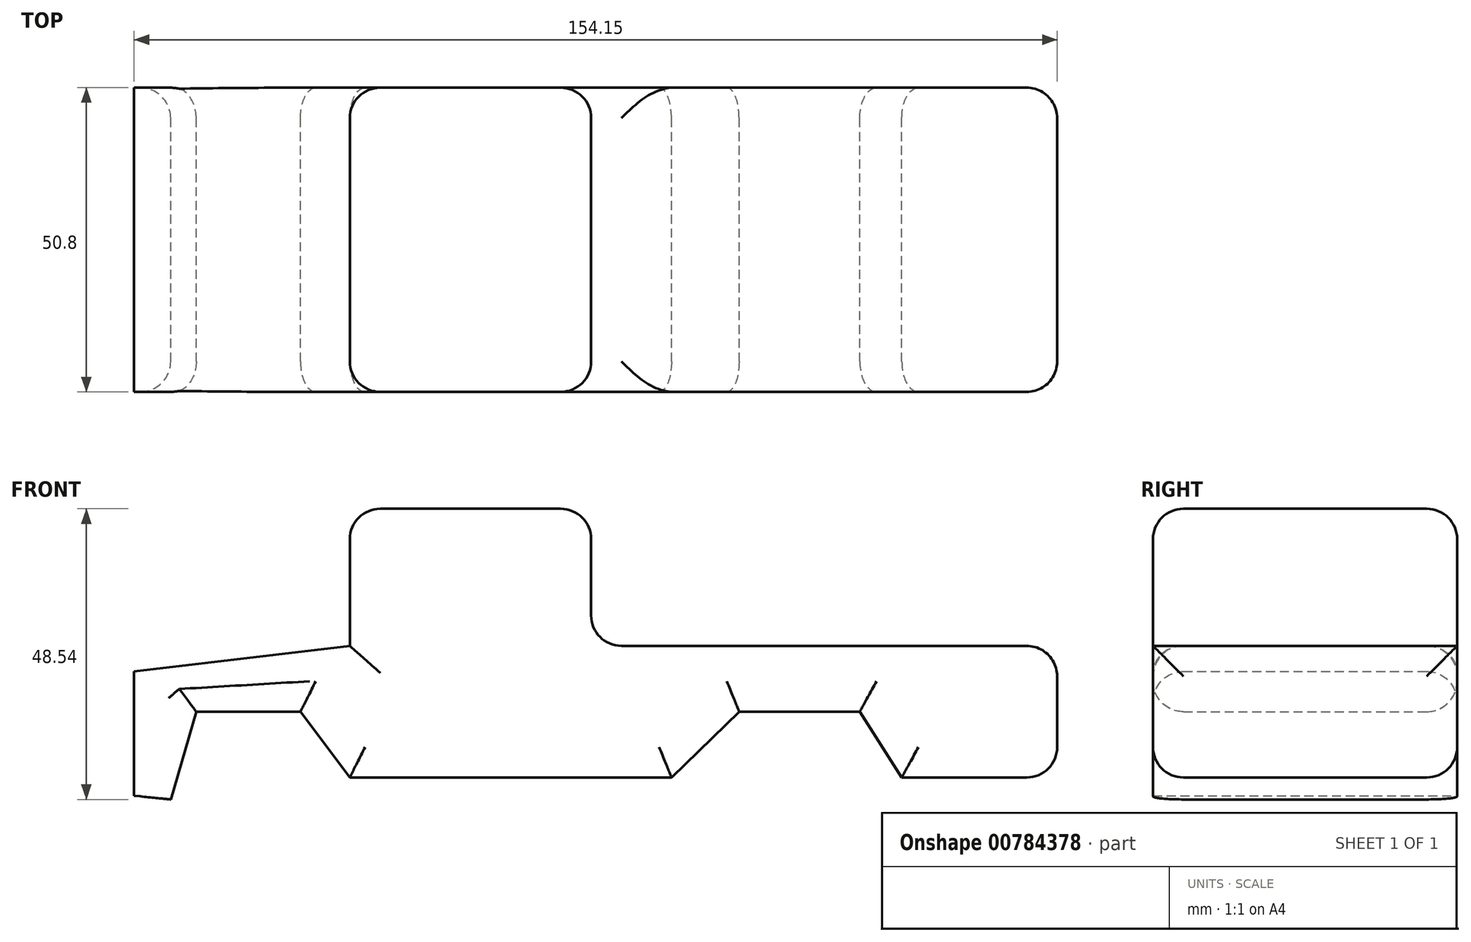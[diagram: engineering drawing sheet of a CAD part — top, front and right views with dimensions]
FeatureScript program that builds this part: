
annotation { "Feature Type Name" : "Feature", "Feature Type Description" : "" }
export const myFeature = defineFeature(function(context is Context, id is Id, definition is map)
    precondition{}
    {
        {
            var Q0;
            Q0=qCreatedBy(makeId("Front.planeOp"),FACE);
            var sketch = newSketch(context, id + "F0", { "sketchPlane" : qUnion([Q0])});
            skLineSegment(sketch, "E0", {"start": v(-106.12, -9.45) * mm, "end": v(-106.12, 11.31) * mm});
            skLineSegment(sketch, "E1", {"start": v(-106.12, 11.31) * mm, "end": v(-70.1, 15.58) * mm});
            skLineSegment(sketch, "E2", {"start": v(-70.1, 15.58) * mm, "end": v(-70.1, 38.48) * mm});
            skLineSegment(sketch, "E3", {"start": v(-70.1, 38.48) * mm, "end": v(-29.81, 38.48) * mm});
            skLineSegment(sketch, "E4", {"start": v(-29.81, 38.48) * mm, "end": v(-29.81, 15.58) * mm});
            skLineSegment(sketch, "E5", {"start": v(-29.81, 15.58) * mm, "end": v(48.03, 15.58) * mm});
            skLineSegment(sketch, "E6", {"start": v(48.03, 15.58) * mm, "end": v(48.03, -6.4) * mm});
            skLineSegment(sketch, "E7", {"start": v(48.03, -6.4) * mm, "end": v(22.08, -6.4) * mm});
            skLineSegment(sketch, "E8", {"start": v(22.08, -6.4) * mm, "end": v(15.06, 4.6) * mm});
            skLineSegment(sketch, "E9", {"start": v(15.06, 4.6) * mm, "end": v(-5.09, 4.6) * mm});
            skLineSegment(sketch, "E10", {"start": v(-5.09, 4.6) * mm, "end": v(-16.38, -6.4) * mm});
            skLineSegment(sketch, "E11", {"start": v(-16.38, -6.4) * mm, "end": v(-70.1, -6.4) * mm});
            skLineSegment(sketch, "E12", {"start": v(-70.1, -6.4) * mm, "end": v(-78.34, 4.6) * mm});
            skLineSegment(sketch, "E13", {"start": v(-78.34, 4.6) * mm, "end": v(-95.74, 4.6) * mm});
            skLineSegment(sketch, "E14", {"start": v(-95.74, 4.6) * mm, "end": v(-100.02, -10.06) * mm});
            skLineSegment(sketch, "E15", {"start": v(-106.12, -9.45) * mm, "end": v(-100.02, -10.06) * mm});
            skSolve(sketch);
        }
        {
            var Q0;
            Q0=makeQuery(id+"F0.imprint","IMPRINT",FACE,{"disambiguationData":[TD([[makeQuery(id+"F0.imprint","IMPRINT",EDGE,{"derivedFrom":sQuery(id+"F0.wireOp",EDGE,"E0")}),-1.0]])]});
            extrude(context, id + "F1", {"entities" : qUnion([Q0]), "depth" : 50.8 * mm, "offsetDistance" : 25.4 * mm});
        }
        {
            var Q0;
            Q0=makeQuery(id+"F1.opExtrude","CAP_EDGE",EDGE,{"disambiguationData":[OSD([sQuery(id+"F0.wireOp",EDGE,"E2")])],"isStart":true});
            var Q1;
            Q1=makeQuery(id+"F1.opExtrude","CAP_EDGE",EDGE,{"disambiguationData":[OSD([sQuery(id+"F0.wireOp",EDGE,"E1")])],"isStart":true});
            var Q2;
            Q2=makeQuery(id+"F1.opExtrude","CAP_EDGE",EDGE,{"disambiguationData":[OSD([sQuery(id+"F0.wireOp",EDGE,"E1")])],"isStart":false});
            var Q3;
            Q3=makeQuery(id+"F1.opExtrude","CAP_EDGE",EDGE,{"disambiguationData":[OSD([sQuery(id+"F0.wireOp",EDGE,"E2")])],"isStart":false});
            var Q4;
            Q4=makeQuery(id+"F1.opExtrude","SWEPT_EDGE",EDGE,{"disambiguationData":[OSD([sQuery(id+"F0.wireOp",EDGE,"E2"),sQuery(id+"F0.wireOp",EDGE,"E3")])]});
            var Q5;
            Q5=makeQuery(id+"F1.opExtrude","SWEPT_EDGE",EDGE,{"disambiguationData":[OSD([sQuery(id+"F0.wireOp",EDGE,"E3"),sQuery(id+"F0.wireOp",EDGE,"E4")])]});
            var Q6;
            Q6=makeQuery(id+"F1.opExtrude","CAP_EDGE",EDGE,{"disambiguationData":[OSD([sQuery(id+"F0.wireOp",EDGE,"E4")])],"isStart":false});
            var Q7;
            Q7=makeQuery(id+"F1.opExtrude","CAP_EDGE",EDGE,{"disambiguationData":[OSD([sQuery(id+"F0.wireOp",EDGE,"E4")])],"isStart":true});
            var Q8;
            Q8=makeQuery(id+"F1.opExtrude","SWEPT_EDGE",EDGE,{"disambiguationData":[OSD([sQuery(id+"F0.wireOp",EDGE,"E4"),sQuery(id+"F0.wireOp",EDGE,"E5")])]});
            var Q9;
            Q9=makeQuery(id+"F1.opExtrude","SWEPT_EDGE",EDGE,{"disambiguationData":[OSD([sQuery(id+"F0.wireOp",EDGE,"E5"),sQuery(id+"F0.wireOp",EDGE,"E6")])]});
            var Q10;
            Q10=makeQuery(id+"F1.opExtrude","CAP_EDGE",EDGE,{"disambiguationData":[OSD([sQuery(id+"F0.wireOp",EDGE,"E6")])],"isStart":true});
            var Q11;
            Q11=makeQuery(id+"F1.opExtrude","CAP_EDGE",EDGE,{"disambiguationData":[OSD([sQuery(id+"F0.wireOp",EDGE,"E6")])],"isStart":false});
            var Q12;
            Q12=makeQuery(id+"F1.opExtrude","SWEPT_EDGE",EDGE,{"disambiguationData":[OSD([sQuery(id+"F0.wireOp",EDGE,"E6"),sQuery(id+"F0.wireOp",EDGE,"E7")])]});
            var Q13;
            Q13=makeQuery(id+"F1.opExtrude","CAP_EDGE",EDGE,{"disambiguationData":[OSD([sQuery(id+"F0.wireOp",EDGE,"E7")])],"isStart":false});
            var Q14;
            Q14=makeQuery(id+"F1.opExtrude","CAP_EDGE",EDGE,{"disambiguationData":[OSD([sQuery(id+"F0.wireOp",EDGE,"E8")])],"isStart":false});
            var Q15;
            Q15=makeQuery(id+"F1.opExtrude","CAP_EDGE",EDGE,{"disambiguationData":[OSD([sQuery(id+"F0.wireOp",EDGE,"E9")])],"isStart":false});
            var Q16;
            Q16=makeQuery(id+"F1.opExtrude","CAP_EDGE",EDGE,{"disambiguationData":[OSD([sQuery(id+"F0.wireOp",EDGE,"E10")])],"isStart":false});
            var Q17;
            Q17=makeQuery(id+"F1.opExtrude","CAP_EDGE",EDGE,{"disambiguationData":[OSD([sQuery(id+"F0.wireOp",EDGE,"E8")])],"isStart":true});
            var Q18;
            Q18=makeQuery(id+"F1.opExtrude","CAP_EDGE",EDGE,{"disambiguationData":[OSD([sQuery(id+"F0.wireOp",EDGE,"E9")])],"isStart":true});
            var Q19;
            Q19=makeQuery(id+"F1.opExtrude","CAP_EDGE",EDGE,{"disambiguationData":[OSD([sQuery(id+"F0.wireOp",EDGE,"E10")])],"isStart":true});
            var Q20;
            Q20=makeQuery(id+"F1.opExtrude","CAP_EDGE",EDGE,{"disambiguationData":[OSD([sQuery(id+"F0.wireOp",EDGE,"E11")])],"isStart":false});
            var Q21;
            Q21=makeQuery(id+"F1.opExtrude","CAP_EDGE",EDGE,{"disambiguationData":[OSD([sQuery(id+"F0.wireOp",EDGE,"E12")])],"isStart":false});
            var Q22;
            Q22=makeQuery(id+"F1.opExtrude","CAP_EDGE",EDGE,{"disambiguationData":[OSD([sQuery(id+"F0.wireOp",EDGE,"E13")])],"isStart":false});
            var Q23;
            Q23=makeQuery(id+"F1.opExtrude","CAP_EDGE",EDGE,{"disambiguationData":[OSD([sQuery(id+"F0.wireOp",EDGE,"E14")])],"isStart":false});
            var Q24;
            Q24=makeQuery(id+"F1.opExtrude","CAP_EDGE",EDGE,{"disambiguationData":[OSD([sQuery(id+"F0.wireOp",EDGE,"E12")])],"isStart":true});
            var Q25;
            Q25=makeQuery(id+"F1.opExtrude","CAP_EDGE",EDGE,{"disambiguationData":[OSD([sQuery(id+"F0.wireOp",EDGE,"E13")])],"isStart":true});
            var Q26;
            Q26=makeQuery(id+"F1.opExtrude","CAP_EDGE",EDGE,{"disambiguationData":[OSD([sQuery(id+"F0.wireOp",EDGE,"E14")])],"isStart":true});
            var Q27;
            Q27=makeQuery(id+"F1.opExtrude","CAP_EDGE",EDGE,{"disambiguationData":[OSD([sQuery(id+"F0.wireOp",EDGE,"E7")])],"isStart":true});
            var Q28;
            Q28=makeQuery(id+"F1.opExtrude","CAP_EDGE",EDGE,{"disambiguationData":[OSD([sQuery(id+"F0.wireOp",EDGE,"E11")])],"isStart":true});
            var Q29;
            Q29=makeQuery(id+"F1.opExtrude","CAP_EDGE",EDGE,{"disambiguationData":[OSD([sQuery(id+"F0.wireOp",EDGE,"E3")])],"isStart":true});
            var Q30;
            Q30=makeQuery(id+"F1.opExtrude","CAP_EDGE",EDGE,{"disambiguationData":[OSD([sQuery(id+"F0.wireOp",EDGE,"E3")])],"isStart":false});
            fillet(context, id + "F2", {"entities" : qUnion([Q0, Q1, Q2, Q3, Q4, Q5, Q6, Q7, Q8, Q9, Q10, Q11, Q12, Q13, Q14, Q15, Q16, Q17, Q18, Q19, Q20, Q21, Q22, Q23, Q24, Q25, Q26, Q27, Q28, Q29, Q30]), "radius" : 5.08 * mm, "tangentPropagation" : true, "allowEdgeOverflow" : false});
        }
    });
